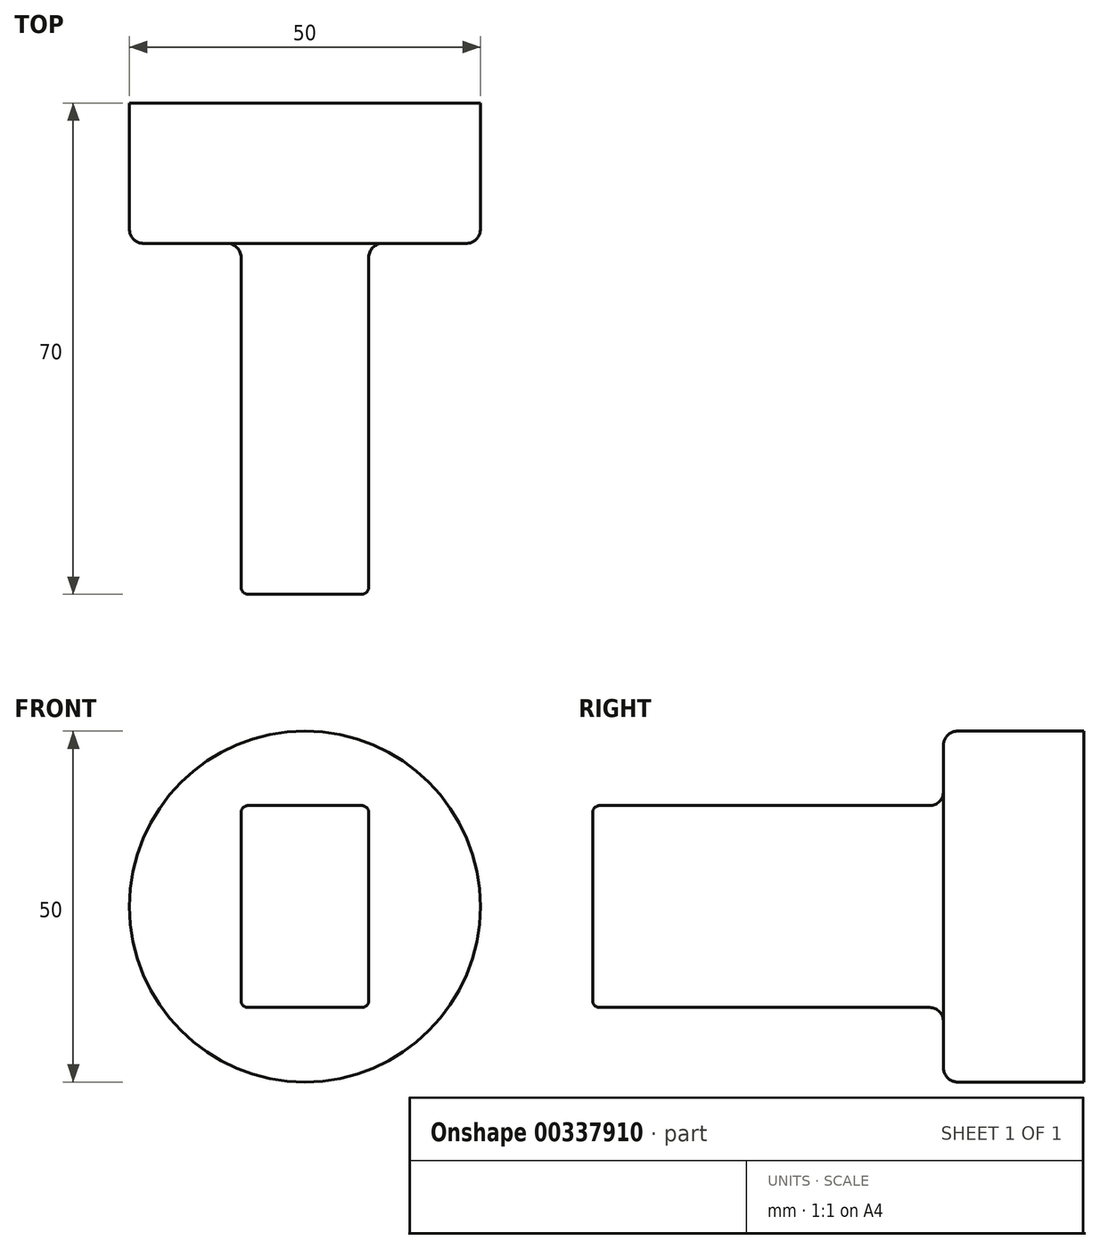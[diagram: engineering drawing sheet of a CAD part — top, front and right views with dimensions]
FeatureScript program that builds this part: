
annotation { "Feature Type Name" : "Feature", "Feature Type Description" : "" }
export const myFeature = defineFeature(function(context is Context, id is Id, definition is map)
    precondition{}
    {
        {
            var Q0;
            Q0=qCreatedBy(makeId("Front.planeOp"),FACE);
            var sketch = newSketch(context, id + "F0", { "sketchPlane" : qUnion([Q0])});
            skCircle(sketch, "E0", {"center": v(0, 0) * mm, "radius": 25 * mm});
            skSolve(sketch);
        }
        {
            var Q0;
            Q0 = qSketchRegion(id + "F0", true);
            extrude(context, id + "F1", {"entities" : qUnion([Q0]), "endBound" : BoundingType.SYMMETRIC, "depth" : 20 * mm});
        }
        {
            var Q0;
            Q0=makeQuery(id+"F1.opExtrude","CAP_FACE",FACE,{"disambiguationData":[OSD([sQuery(id+"F0.wireOp",EDGE,"E0")])],"isStart":false});
            var sketch = newSketch(context, id + "F2", { "sketchPlane" : qUnion([Q0])});
            skLineSegment(sketch, "E1.bottom", {"start": v(9.1, 14.39) * mm, "end": v(-9.1, 14.39) * mm});
            skLineSegment(sketch, "E1.top", {"start": v(9.1, -14.39) * mm, "end": v(-9.1, -14.39) * mm});
            skLineSegment(sketch, "E1.left", {"start": v(9.1, 14.39) * mm, "end": v(9.1, -14.39) * mm});
            skLineSegment(sketch, "E1.right", {"start": v(-9.1, 14.39) * mm, "end": v(-9.1, -14.39) * mm});
            skPoint(sketch, "E1.middle", {"position": v(0, 0) * mm});
            skSolve(sketch);
        }
        {
            var Q0;
            Q0=makeQuery(id+"F2.imprint","IMPRINT",FACE,{"disambiguationData":[TD([[makeQuery(id+"F2.imprint","IMPRINT",EDGE,{"derivedFrom":sQuery(id+"F2.wireOp",EDGE,"E1.bottom")}),1.0]])]});
            extrude(context, id + "F3", {"entities" : qUnion([Q0]), "operationType" : NewBodyOperationType.ADD, "depth" : 50 * mm});
        }
        {
            var Q0;
            Q0=makeQuery(id+"F3.opExtrude","CAP_EDGE",EDGE,{"disambiguationData":[OSD([sQuery(id+"F2.wireOp",EDGE,"E1.bottom")])],"isStart":true});
            var Q1;
            Q1=makeQuery(id+"F3.opExtrude","CAP_EDGE",EDGE,{"disambiguationData":[OSD([sQuery(id+"F2.wireOp",EDGE,"E1.left")])],"isStart":true});
            var Q2;
            Q2=makeQuery(id+"F3.opExtrude","CAP_EDGE",EDGE,{"disambiguationData":[OSD([sQuery(id+"F2.wireOp",EDGE,"E1.right")])],"isStart":true});
            var Q3;
            Q3=makeQuery(id+"F3.opExtrude","CAP_EDGE",EDGE,{"disambiguationData":[OSD([sQuery(id+"F2.wireOp",EDGE,"E1.top")])],"isStart":true});
            var Q4;
            Q4=makeQuery(id+"F3.opExtrude","SWEPT_EDGE",EDGE,{"disambiguationData":[OSD([sQuery(id+"F2.wireOp",EDGE,"E1.top"),sQuery(id+"F2.wireOp",EDGE,"E1.right")])]});
            var Q5;
            Q5=makeQuery(id+"F3.opExtrude","SWEPT_EDGE",EDGE,{"disambiguationData":[OSD([sQuery(id+"F2.wireOp",EDGE,"E1.bottom"),sQuery(id+"F2.wireOp",EDGE,"E1.right")])]});
            var Q6;
            Q6=makeQuery(id+"F3.opExtrude","SWEPT_EDGE",EDGE,{"disambiguationData":[OSD([sQuery(id+"F2.wireOp",EDGE,"E1.bottom"),sQuery(id+"F2.wireOp",EDGE,"E1.left")])]});
            var Q7;
            Q7=makeQuery(id+"F3.opExtrude","SWEPT_EDGE",EDGE,{"disambiguationData":[OSD([sQuery(id+"F2.wireOp",EDGE,"E1.top"),sQuery(id+"F2.wireOp",EDGE,"E1.left")])]});
            var Q8;
            Q8=makeQuery(id+"F3.opExtrude","CAP_EDGE",EDGE,{"disambiguationData":[OSD([sQuery(id+"F2.wireOp",EDGE,"E1.left")])],"isStart":false});
            var Q9;
            Q9=makeQuery(id+"F3.opExtrude","CAP_EDGE",EDGE,{"disambiguationData":[OSD([sQuery(id+"F2.wireOp",EDGE,"E1.right")])],"isStart":false});
            var Q10;
            Q10=makeQuery(id+"F3.opExtrude","CAP_EDGE",EDGE,{"disambiguationData":[OSD([sQuery(id+"F2.wireOp",EDGE,"E1.bottom")])],"isStart":false});
            var Q11;
            Q11=makeQuery(id+"F3.opExtrude","CAP_EDGE",EDGE,{"disambiguationData":[OSD([sQuery(id+"F2.wireOp",EDGE,"E1.top")])],"isStart":false});
            fillet(context, id + "F4", {"entities" : qUnion([Q0, Q1, Q2, Q3, Q4, Q5, Q6, Q7, Q8, Q9, Q10, Q11]), "radius" : 1 * mm, "tangentPropagation" : true, "allowEdgeOverflow" : false});
        }
        {
            var Q0;
            Q0=makeQuery(id+"F1.opExtrude","CAP_FACE",FACE,{"disambiguationData":[OSD([sQuery(id+"F0.wireOp",EDGE,"E0")])],"isStart":false});
            fillet(context, id + "F5", {"entities" : qUnion([Q0]), "radius" : 2 * mm, "tangentPropagation" : true, "allowEdgeOverflow" : false});
        }
    });
